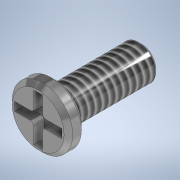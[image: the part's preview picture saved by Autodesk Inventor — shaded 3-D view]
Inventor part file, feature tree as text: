
AUTODESK INVENTOR PART (.ipt)
format: ipt  version: 2021 (Build 250183000, 183)  size: 157,696 bytes
history: native  units: mm
features: extrude x3, sketch x3, chamfer x2, other x1, thread x1, fillet x1
ambient origin geometry x8: Origin, YZ Plane, XZ Plane, XY Plane, X Axis, Y Axis, Z Axis, Center Point
bodies: Body1 (feature_tree)
feature tree (11):
  other  "Sólido1"
  extrude  "Extrusão1"  Depth=5.0mm TaperAngle=0.0deg
  extrude  "Extrusão2"  Depth=1.0mm TaperAngle=0.0deg
  extrude  "Extrusão3"  Depth=0.5mm
  thread  "Rosca1"  [1 undecoded]
  fillet  "Arredondamento2"  Radius=2.75mm
  chamfer  "Chanfro1"  Distance=0.6mm
  chamfer  "Chanfro2"  Distance=15.255mm
  sketch  "Esboço1"  dims[d0=2.0mm d1=5.0mm d2=0.0mm]
  sketch  "Esboço2"  dims[d3=3.5mm d4=1.0mm d5=0.0mm]
  sketch  "Esboço3"  dims[d6=0.5mm d7=0.5mm d8=2.75mm d9=2.75mm d10=0.6mm d11=0.0mm d13=15.255mm d14=0.0mm d15=0.2mm d16=0.25mm d17=2.0mm d18=45.0deg d19=0.2mm d20=2.0mm d21=45.0deg]
note: 1 required parameter value undecoded (feature->parameter linkage not recoverable at this tier; creation-order binding heuristic only, values carry confidence <= 0.55)
